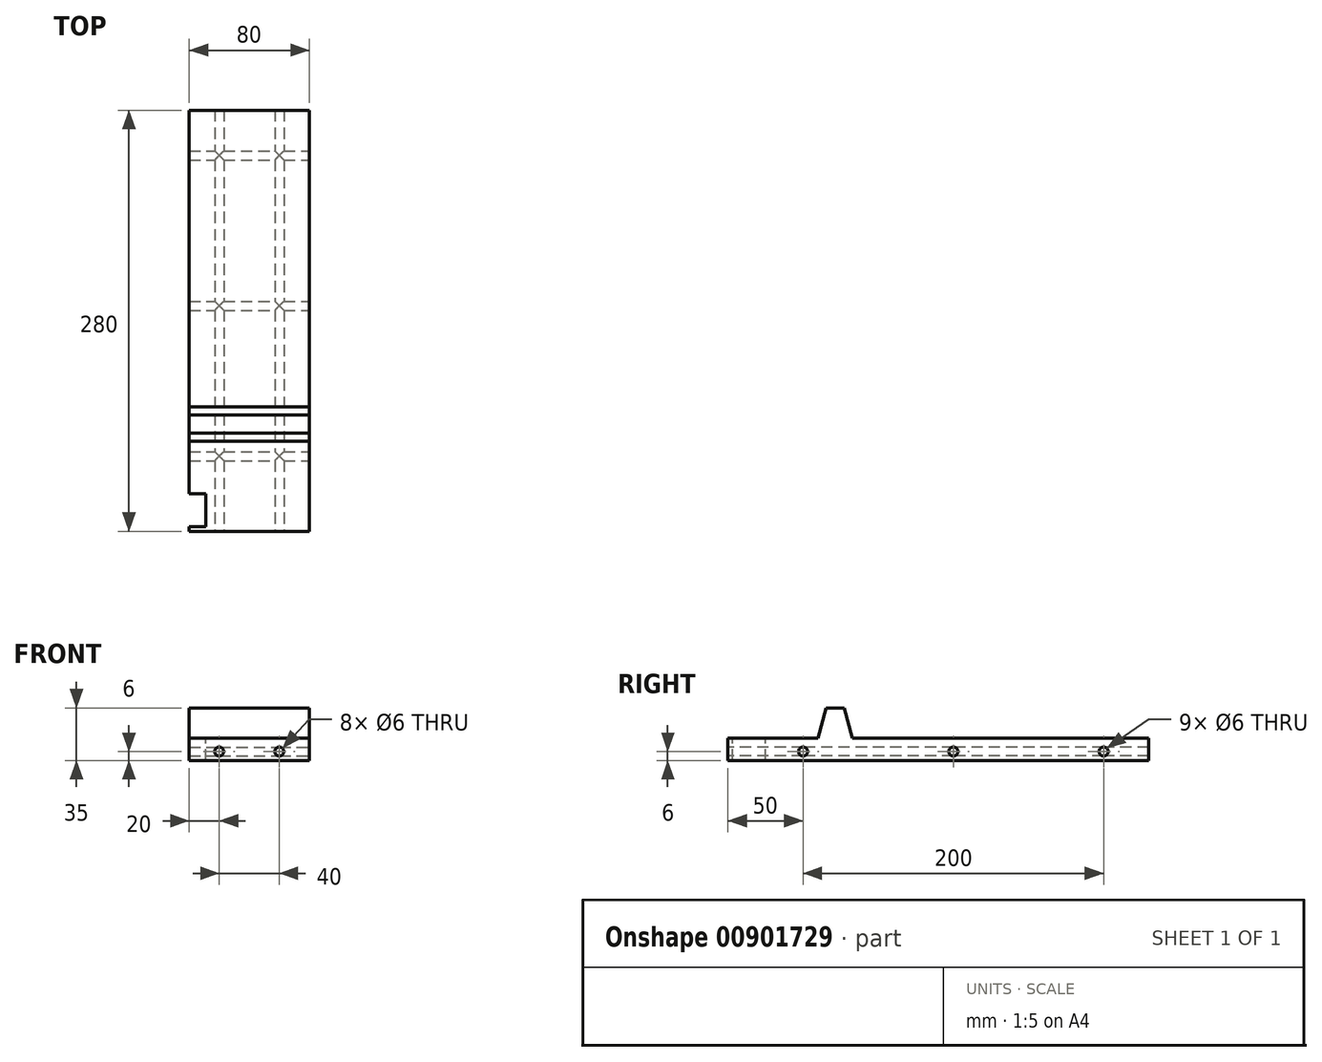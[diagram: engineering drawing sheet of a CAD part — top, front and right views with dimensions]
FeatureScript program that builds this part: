
annotation { "Feature Type Name" : "Feature", "Feature Type Description" : "" }
export const myFeature = defineFeature(function(context is Context, id is Id, definition is map)
    precondition{}
    {
        {
            var Q0;
            Q0=qCreatedBy(makeId("Top.planeOp"),FACE);
            var sketch = newSketch(context, id + "F0", { "sketchPlane" : qUnion([Q0])});
            skLineSegment(sketch, "E0.bottom", {"start": v(0, 0) * mm, "end": v(80, 0) * mm});
            skLineSegment(sketch, "E0.top", {"start": v(0, 280) * mm, "end": v(80, 280) * mm});
            skLineSegment(sketch, "E0.left", {"start": v(0, 0) * mm, "end": v(0, 280) * mm});
            skLineSegment(sketch, "E0.right", {"start": v(80, 0) * mm, "end": v(80, 280) * mm});
            skSolve(sketch);
        }
        {
            var Q0;
            Q0=makeQuery(id+"F0.imprint","IMPRINT",FACE,{"disambiguationData":[TD([[makeQuery(id+"F0.imprint","IMPRINT",EDGE,{"derivedFrom":sQuery(id+"F0.wireOp",EDGE,"E0.bottom")}),1.0]])]});
            extrude(context, id + "F1", {"entities" : qUnion([Q0]), "depth" : 15 * mm, "offsetDistance" : 25 * mm});
        }
        {
            var Q0;
            Q0=makeQuery(id+"F1.opExtrude","SWEPT_FACE",FACE,{"disambiguationData":[OSD([sQuery(id+"F0.wireOp",EDGE,"E0.right")])]});
            var sketch = newSketch(context, id + "F2", { "sketchPlane" : qUnion([Q0])});
            skLineSegment(sketch, "E1", {"start": v(60, 15) * mm, "end": v(65.36, 35) * mm});
            skLineSegment(sketch, "E2", {"start": v(65.36, 35) * mm, "end": v(77.36, 35) * mm});
            skLineSegment(sketch, "E3", {"start": v(77.36, 35) * mm, "end": v(82.72, 15) * mm});
            skLineSegment(sketch, "E4", {"start": v(60, 15) * mm, "end": v(82.72, 15) * mm});
            skSolve(sketch);
        }
        {
            var Q0;
            Q0 = qSketchRegion(id + "F2", true);
            extrude(context, id + "F3", {"entities" : qUnion([Q0]), "operationType" : NewBodyOperationType.ADD, "oppositeDirection" : true, "depth" : 80 * mm, "offsetDistance" : 25 * mm});
        }
        {
            var Q0;
            {var subQ1=sQuery(id+"F0.wireOp",EDGE,"E0.left");var subQ2=sQuery(id+"F0.wireOp",EDGE,"E0.right");var subQ3=sQuery(id+"F0.wireOp",EDGE,"E0.bottom");Q0=makeQuery(id+"F3.boolean.opBoolean","SPLIT",FACE,{"disambiguationData":[TD([makeQuery(id+"F1.opExtrude","SWEPT_FACE",FACE,{"disambiguationData":[OSD([subQ3])]})])],"derivedFrom":makeQuery(id+"F1.opExtrude","CAP_FACE",FACE,{"disambiguationData":[OSD([subQ3,sQuery(id+"F0.wireOp",EDGE,"E0.top"),subQ1,subQ2])],"isStart":false})});}
            var sketch = newSketch(context, id + "F4", { "sketchPlane" : qUnion([Q0])});
            skLineSegment(sketch, "E5", {"start": v(11, 25) * mm, "end": v(0, 25) * mm});
            skLineSegment(sketch, "E6", {"start": v(11, 25) * mm, "end": v(11, 3) * mm});
            skLineSegment(sketch, "E7", {"start": v(11, 3) * mm, "end": v(0, 3) * mm});
            skLineSegment(sketch, "E8", {"start": v(0, 3) * mm, "end": v(0, 25) * mm});
            skSolve(sketch);
        }
        {
            var Q0;
            Q0 = qSketchRegion(id + "F4", true);
            extrude(context, id + "F5", {"entities" : qUnion([Q0]), "operationType" : NewBodyOperationType.REMOVE, "endBound" : BoundingType.UP_TO_NEXT, "oppositeDirection" : true, "depth" : 25 * mm, "offsetDistance" : 25 * mm});
        }
        {
            var Q0;
            Q0=makeQuery(id+"F1.opExtrude","SWEPT_FACE",FACE,{"disambiguationData":[OSD([sQuery(id+"F0.wireOp",EDGE,"E0.bottom")])]});
            var sketch = newSketch(context, id + "F6", { "sketchPlane" : qUnion([Q0])});
            skSolve(sketch);
        }
        {
            var Q0;
            {var subQ0=sQuery(id+"F0.wireOp",EDGE,"E0.bottom");Q0=makeQuery(id+"F6.imprint","IMPRINT",FACE,{"disambiguationData":[TD([[makeQuery(id+"F6.imprint","IMPRINT",EDGE,{"derivedFrom":makeQuery(id+"F1.opExtrude","CAP_EDGE",EDGE,{"disambiguationData":[OSD([subQ0])],"isStart":true})}),1.0]])]});}
            var sketch = newSketch(context, id + "F7", { "sketchPlane" : qUnion([Q0])});
            skCircle(sketch, "E9", {"center": v(60, 6) * mm, "radius": 3 * mm});
            skCircle(sketch, "E10", {"center": v(-491.18, 5.33) * mm, "radius": 6.56 * mm});
            skCircle(sketch, "E11", {"center": v(20, 6) * mm, "radius": 3 * mm});
            skSolve(sketch);
        }
        {
            var Q0;
            Q0 = qSketchRegion(id + "F7", true);
            extrude(context, id + "F8", {"entities" : qUnion([Q0]), "operationType" : NewBodyOperationType.REMOVE, "endBound" : BoundingType.THROUGH_ALL, "oppositeDirection" : true, "depth" : 25 * mm, "offsetDistance" : 25 * mm});
        }
        {
            var Q0;
            Q0=makeQuery(id+"F3.boolean.opBoolean","MERGE",FACE,{"derivedFrom":[makeQuery(id+"F1.opExtrude","SWEPT_FACE",FACE,{"disambiguationData":[OSD([sQuery(id+"F0.wireOp",EDGE,"E0.right")])]}),makeQuery(id+"F3.opExtrude","CAP_FACE",FACE,{"disambiguationData":[OSD([sQuery(id+"F2.wireOp",EDGE,"E1"),sQuery(id+"F2.wireOp",EDGE,"E2"),sQuery(id+"F2.wireOp",EDGE,"E3"),sQuery(id+"F2.wireOp",EDGE,"E4")])],"isStart":true})]});
            var sketch = newSketch(context, id + "F9", { "sketchPlane" : qUnion([Q0])});
            skCircle(sketch, "E12", {"center": v(50, 6) * mm, "radius": 3 * mm});
            skCircle(sketch, "E13", {"center": v(250, 6) * mm, "radius": 3 * mm});
            skCircle(sketch, "E14", {"center": v(150, 6) * mm, "radius": 3 * mm});
            skSolve(sketch);
        }
        {
            var Q0;
            Q0=makeQuery(id+"F9.imprint","IMPRINT",FACE,{"disambiguationData":[TD([[makeQuery(id+"F9.imprint","IMPRINT",EDGE,{"derivedFrom":sQuery(id+"F9.wireOp",EDGE,"E12")}),1.0]])]});
            var Q1;
            Q1=makeQuery(id+"F9.imprint","IMPRINT",FACE,{"disambiguationData":[TD([[makeQuery(id+"F9.imprint","IMPRINT",EDGE,{"derivedFrom":sQuery(id+"F9.wireOp",EDGE,"E14")}),1.0]])]});
            var Q2;
            Q2=makeQuery(id+"F9.imprint","IMPRINT",FACE,{"disambiguationData":[TD([[makeQuery(id+"F9.imprint","IMPRINT",EDGE,{"derivedFrom":sQuery(id+"F9.wireOp",EDGE,"E13")}),1.0]])]});
            extrude(context, id + "F10", {"entities" : qUnion([Q0, Q1, Q2]), "operationType" : NewBodyOperationType.REMOVE, "endBound" : BoundingType.THROUGH_ALL, "oppositeDirection" : true, "depth" : 25 * mm, "offsetDistance" : 25 * mm});
        }
    });
